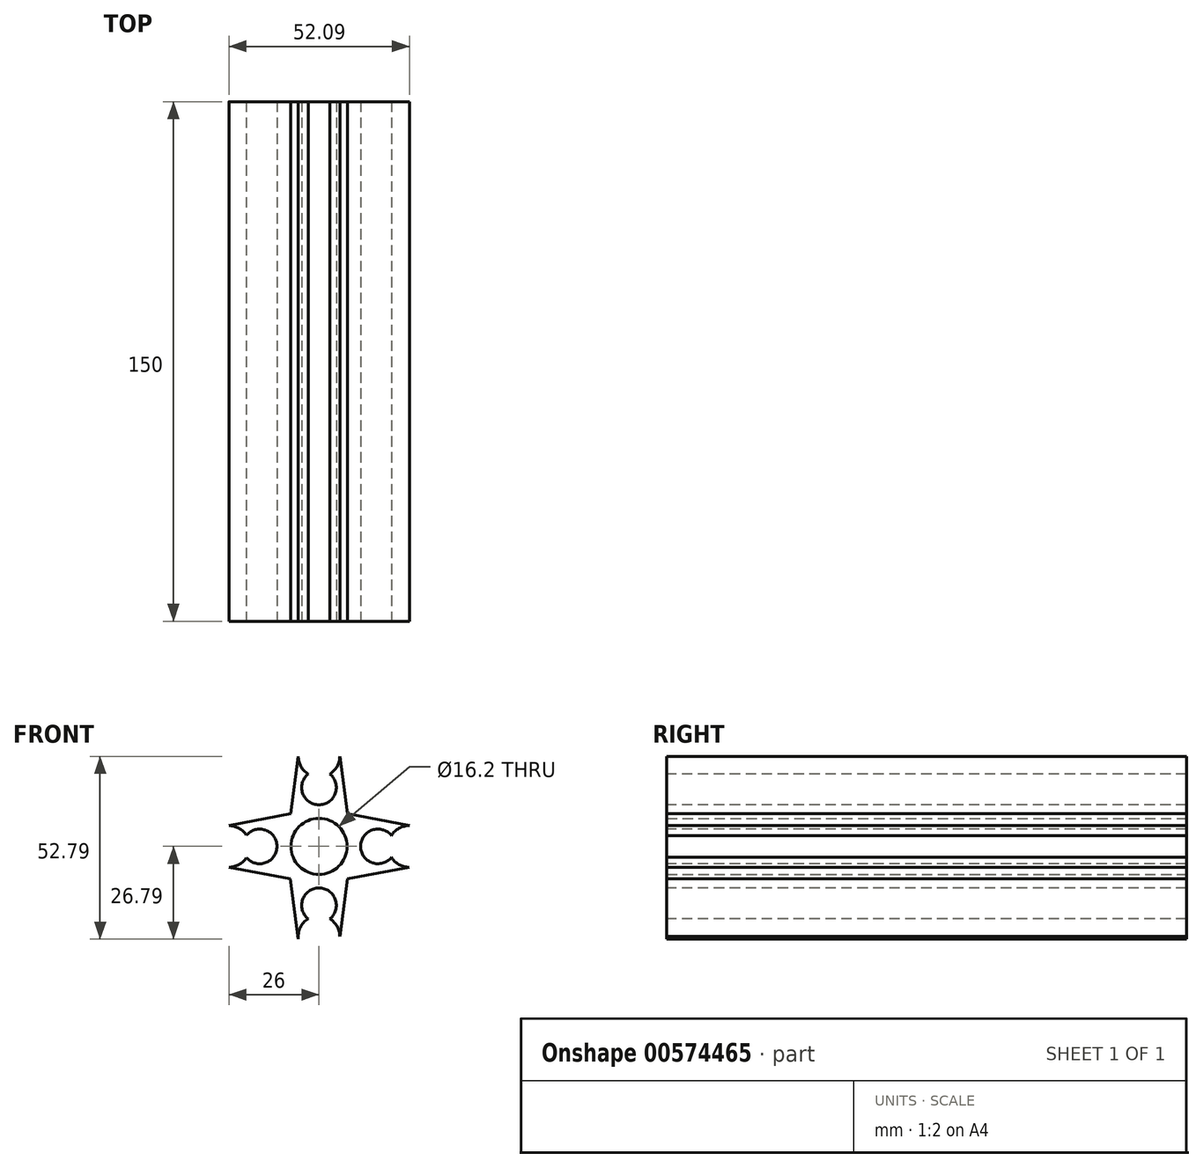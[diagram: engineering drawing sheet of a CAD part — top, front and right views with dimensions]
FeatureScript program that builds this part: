
annotation { "Feature Type Name" : "Feature", "Feature Type Description" : "" }
export const myFeature = defineFeature(function(context is Context, id is Id, definition is map)
    precondition{}
    {
        {
            var Q0;
            Q0=qCreatedBy(makeId("Front.planeOp"),FACE);
            var sketch = newSketch(context, id + "F0", { "sketchPlane" : qUnion([Q0])});
            skLineSegment(sketch, "E0", {"start": v(0, 0) * mm, "end": v(32, 0) * mm});
            skLineSegment(sketch, "E1", {"start": v(0, 0) * mm, "end": v(-32, 0) * mm});
            skLineSegment(sketch, "E2", {"start": v(0, 0) * mm, "end": v(0, 32) * mm});
            skLineSegment(sketch, "E3", {"start": v(0, 0) * mm, "end": v(0, -32) * mm});
            skCircle(sketch, "E4", {"center": v(0, 0) * mm, "radius": 8.05 * mm});
            skLineSegment(sketch, "E5", {"start": v(0, 32) * mm, "end": v(0, 26) * mm});
            skLineSegment(sketch, "E6", {"start": v(32, 0) * mm, "end": v(26, 0) * mm});
            skLineSegment(sketch, "E7", {"start": v(-32, 0) * mm, "end": v(-26, 0) * mm});
            skLineSegment(sketch, "E8", {"start": v(0, -32) * mm, "end": v(0, -26) * mm});
            skCircle(sketch, "E9", {"center": v(0, -26) * mm, "radius": 6 * mm});
            skCircle(sketch, "E10", {"center": v(26, 0) * mm, "radius": 6 * mm});
            skCircle(sketch, "E11", {"center": v(0, 0) * mm, "radius": 12.5 * mm});
            skLineSegment(sketch, "E12", {"start": v(-6, 26) * mm, "end": v(-8.17, 9.46) * mm});
            skLineSegment(sketch, "E13", {"start": v(-26, -6) * mm, "end": v(-8.26, -9.39) * mm});
            skLineSegment(sketch, "E14", {"start": v(6, -26) * mm, "end": v(8.25, -9.39) * mm});
            skLineSegment(sketch, "E15", {"start": v(8.25, -9.39) * mm, "end": v(26, -6) * mm});
            skLineSegment(sketch, "E16", {"start": v(6, 26) * mm, "end": v(8.23, 9.4) * mm});
            skCircle(sketch, "E17", {"center": v(0, 26) * mm, "radius": 6 * mm});
            skLineSegment(sketch, "E18", {"start": v(0, 0) * mm, "end": v(-14.25, 0) * mm});
            skCircle(sketch, "E19", {"center": v(-26, 0) * mm, "radius": 6 * mm});
            skLineSegment(sketch, "E20", {"start": v(-8.17, 9.46) * mm, "end": v(-25.97, 6) * mm});
            skLineSegment(sketch, "E21", {"start": v(-8.26, -9.39) * mm, "end": v(-5.95, -26.79) * mm});
            skLineSegment(sketch, "E22", {"start": v(8.23, 9.4) * mm, "end": v(26.09, 6) * mm});
            skSolve(sketch);
        }
        {
            var Q0;
            {var subQ0=sQuery(id+"F0.wireOp",EDGE,"E20");Q0=makeQuery(id+"F0.imprint","IMPRINT",FACE,{"disambiguationData":[TD([[makeQuery(id+"F0.imprint","IMPRINT",EDGE,{"derivedFrom":subQ0}),1.0]])]});}
            var Q1;
            {var subQ0=sQuery(id+"F0.wireOp",EDGE,"E7");Q1=makeQuery(id+"F0.imprint","IMPRINT",FACE,{"disambiguationData":[TD([[makeQuery(id+"F0.imprint","IMPRINT",EDGE,{"derivedFrom":subQ0}),1.0]])]});}
            var Q2;
            {var subQ0=sQuery(id+"F0.wireOp",EDGE,"E7");Q2=makeQuery(id+"F0.imprint","IMPRINT",FACE,{"disambiguationData":[TD([[makeQuery(id+"F0.imprint","IMPRINT",EDGE,{"derivedFrom":subQ0}),-1.0]])]});}
            var Q3;
            {var subQ5=sQuery(id+"F0.wireOp",EDGE,"E13");Q3=makeQuery(id+"F0.imprint","IMPRINT",FACE,{"disambiguationData":[TD([[makeQuery(id+"F0.imprint","IMPRINT",EDGE,{"derivedFrom":subQ5}),1.0]])]});}
            var Q4;
            {var subQ2=sQuery(id+"F0.wireOp",EDGE,"E3");var subQ6=sQuery(id+"F0.wireOp",EDGE,"E4");var subQ7=makeQuery(id+"F0.imprint","INTERSECT",VERTEX,{"derivedFrom":[subQ2,subQ6]});Q4=makeQuery(id+"F0.imprint","IMPRINT",FACE,{"disambiguationData":[TD([[makeQuery(id+"F0.imprint","IMPRINT",EDGE,{"disambiguationData":[TD([[subQ7,-1.0]])],"derivedFrom":subQ2}),-1.0]])]});}
            var Q5;
            {var subQ4=sQuery(id+"F0.wireOp",EDGE,"E4");var subQ5=sQuery(id+"F0.wireOp",EDGE,"E2");var subQ6=makeQuery(id+"F0.imprint","INTERSECT",VERTEX,{"derivedFrom":[subQ5,subQ4]});Q5=makeQuery(id+"F0.imprint","IMPRINT",FACE,{"disambiguationData":[TD([[makeQuery(id+"F0.imprint","IMPRINT",EDGE,{"disambiguationData":[TD([[subQ6,-1.0]])],"derivedFrom":subQ5}),1.0]])]});}
            var Q6;
            {var subQ5=sQuery(id+"F0.wireOp",EDGE,"E12");Q6=makeQuery(id+"F0.imprint","IMPRINT",FACE,{"disambiguationData":[TD([[makeQuery(id+"F0.imprint","IMPRINT",EDGE,{"derivedFrom":subQ5}),1.0]])]});}
            var Q7;
            {var subQ5=sQuery(id+"F0.wireOp",EDGE,"E16");Q7=makeQuery(id+"F0.imprint","IMPRINT",FACE,{"disambiguationData":[TD([[makeQuery(id+"F0.imprint","IMPRINT",EDGE,{"derivedFrom":subQ5}),-1.0]])]});}
            var Q8;
            {var subQ0=sQuery(id+"F0.wireOp",EDGE,"E5");Q8=makeQuery(id+"F0.imprint","IMPRINT",FACE,{"disambiguationData":[TD([[makeQuery(id+"F0.imprint","IMPRINT",EDGE,{"derivedFrom":subQ0}),1.0]])]});}
            var Q9;
            {var subQ0=sQuery(id+"F0.wireOp",EDGE,"E5");Q9=makeQuery(id+"F0.imprint","IMPRINT",FACE,{"disambiguationData":[TD([[makeQuery(id+"F0.imprint","IMPRINT",EDGE,{"derivedFrom":subQ0}),-1.0]])]});}
            var Q10;
            {var subQ5=sQuery(id+"F0.wireOp",EDGE,"E22");Q10=makeQuery(id+"F0.imprint","IMPRINT",FACE,{"disambiguationData":[TD([[makeQuery(id+"F0.imprint","IMPRINT",EDGE,{"derivedFrom":subQ5}),-1.0]])]});}
            var Q11;
            {var subQ0=sQuery(id+"F0.wireOp",EDGE,"E6");Q11=makeQuery(id+"F0.imprint","IMPRINT",FACE,{"disambiguationData":[TD([[makeQuery(id+"F0.imprint","IMPRINT",EDGE,{"derivedFrom":subQ0}),-1.0]])]});}
            var Q12;
            {var subQ0=sQuery(id+"F0.wireOp",EDGE,"E6");Q12=makeQuery(id+"F0.imprint","IMPRINT",FACE,{"disambiguationData":[TD([[makeQuery(id+"F0.imprint","IMPRINT",EDGE,{"derivedFrom":subQ0}),1.0]])]});}
            var Q13;
            {var subQ2=sQuery(id+"F0.wireOp",EDGE,"E0");var subQ4=sQuery(id+"F0.wireOp",EDGE,"E4");var subQ5=makeQuery(id+"F0.imprint","INTERSECT",VERTEX,{"derivedFrom":[subQ2,subQ4]});Q13=makeQuery(id+"F0.imprint","IMPRINT",FACE,{"disambiguationData":[TD([[makeQuery(id+"F0.imprint","IMPRINT",EDGE,{"disambiguationData":[TD([[subQ5,-1.0]])],"derivedFrom":subQ2}),1.0]])]});}
            var Q14;
            {var subQ1=sQuery(id+"F0.wireOp",EDGE,"E0");var subQ3=sQuery(id+"F0.wireOp",EDGE,"E4");var subQ4=makeQuery(id+"F0.imprint","INTERSECT",VERTEX,{"derivedFrom":[subQ1,subQ3]});Q14=makeQuery(id+"F0.imprint","IMPRINT",FACE,{"disambiguationData":[TD([[makeQuery(id+"F0.imprint","IMPRINT",EDGE,{"disambiguationData":[TD([[subQ4,-1.0]])],"derivedFrom":subQ3}),1.0]])]});}
            var Q15;
            {var subQ1=sQuery(id+"F0.wireOp",EDGE,"E2");var subQ3=sQuery(id+"F0.wireOp",EDGE,"E4");var subQ4=makeQuery(id+"F0.imprint","INTERSECT",VERTEX,{"derivedFrom":[subQ1,subQ3]});Q15=makeQuery(id+"F0.imprint","IMPRINT",FACE,{"disambiguationData":[TD([[makeQuery(id+"F0.imprint","IMPRINT",EDGE,{"disambiguationData":[TD([[subQ4,-1.0]])],"derivedFrom":subQ3}),1.0]])]});}
            var Q16;
            {var subQ1=sQuery(id+"F0.wireOp",EDGE,"E3");var subQ3=sQuery(id+"F0.wireOp",EDGE,"E4");var subQ4=makeQuery(id+"F0.imprint","INTERSECT",VERTEX,{"derivedFrom":[subQ1,subQ3]});Q16=makeQuery(id+"F0.imprint","IMPRINT",FACE,{"disambiguationData":[TD([[makeQuery(id+"F0.imprint","IMPRINT",EDGE,{"disambiguationData":[TD([[subQ4,1.0]])],"derivedFrom":subQ3}),1.0]])]});}
            var Q17;
            {var subQ1=sQuery(id+"F0.wireOp",EDGE,"E0");var subQ3=sQuery(id+"F0.wireOp",EDGE,"E4");var subQ4=makeQuery(id+"F0.imprint","INTERSECT",VERTEX,{"derivedFrom":[subQ1,subQ3]});Q17=makeQuery(id+"F0.imprint","IMPRINT",FACE,{"disambiguationData":[TD([[makeQuery(id+"F0.imprint","IMPRINT",EDGE,{"disambiguationData":[TD([[subQ4,1.0]])],"derivedFrom":subQ3}),1.0]])]});}
            var Q18;
            {var subQ0=sQuery(id+"F0.wireOp",EDGE,"E4");var subQ1=sQuery(id+"F0.wireOp",EDGE,"E0");var subQ2=makeQuery(id+"F0.imprint","INTERSECT",VERTEX,{"derivedFrom":[subQ1,subQ0]});Q18=makeQuery(id+"F0.imprint","IMPRINT",FACE,{"disambiguationData":[TD([[makeQuery(id+"F0.imprint","IMPRINT",EDGE,{"disambiguationData":[TD([[subQ2,-1.0]])],"derivedFrom":subQ1}),-1.0]])]});}
            var Q19;
            {var subQ5=sQuery(id+"F0.wireOp",EDGE,"E15");Q19=makeQuery(id+"F0.imprint","IMPRINT",FACE,{"disambiguationData":[TD([[makeQuery(id+"F0.imprint","IMPRINT",EDGE,{"derivedFrom":subQ5}),1.0]])]});}
            var Q20;
            {var subQ5=sQuery(id+"F0.wireOp",EDGE,"E21");Q20=makeQuery(id+"F0.imprint","IMPRINT",FACE,{"disambiguationData":[TD([[makeQuery(id+"F0.imprint","IMPRINT",EDGE,{"derivedFrom":subQ5}),1.0]])]});}
            var Q21;
            {var subQ5=sQuery(id+"F0.wireOp",EDGE,"E14");Q21=makeQuery(id+"F0.imprint","IMPRINT",FACE,{"disambiguationData":[TD([[makeQuery(id+"F0.imprint","IMPRINT",EDGE,{"derivedFrom":subQ5}),1.0]])]});}
            var Q22;
            {var subQ0=sQuery(id+"F0.wireOp",EDGE,"E8");Q22=makeQuery(id+"F0.imprint","IMPRINT",FACE,{"disambiguationData":[TD([[makeQuery(id+"F0.imprint","IMPRINT",EDGE,{"derivedFrom":subQ0}),1.0]])]});}
            var Q23;
            {var subQ0=sQuery(id+"F0.wireOp",EDGE,"E8");Q23=makeQuery(id+"F0.imprint","IMPRINT",FACE,{"disambiguationData":[TD([[makeQuery(id+"F0.imprint","IMPRINT",EDGE,{"derivedFrom":subQ0}),-1.0]])]});}
            extrude(context, id + "F1", {"entities" : qUnion([Q0, Q1, Q2, Q3, Q4, Q5, Q6, Q7, Q8, Q9, Q10, Q11, Q12, Q13, Q14, Q15, Q16, Q17, Q18, Q19, Q20, Q21, Q22, Q23]), "depth" : 150 * mm, "offsetDistance" : 25 * mm});
        }
        {
            var Q0;
            Q0=qCreatedBy(makeId("Front.planeOp"),FACE);
            var sketch = newSketch(context, id + "F2", { "sketchPlane" : qUnion([Q0])});
            skCircle(sketch, "E23", {"center": v(0, 0) * mm, "radius": 8.1 * mm});
            skCircle(sketch, "E24", {"center": v(0, 26) * mm, "radius": 1.6 * mm});
            skCircle(sketch, "E25", {"center": v(26, 0) * mm, "radius": 1.6 * mm});
            skCircle(sketch, "E26", {"center": v(0, -26) * mm, "radius": 1.6 * mm});
            skCircle(sketch, "E27", {"center": v(-26, 0) * mm, "radius": 1.6 * mm});
            skSolve(sketch);
        }
        {
            var Q0;
            Q0=makeQuery(id+"F2.imprint","IMPRINT",FACE,{"disambiguationData":[TD([[makeQuery(id+"F2.imprint","IMPRINT",EDGE,{"derivedFrom":sQuery(id+"F2.wireOp",EDGE,"E23")}),1.0]])]});
            var Q1;
            Q1=makeQuery(id+"F2.imprint","IMPRINT",FACE,{"disambiguationData":[TD([[makeQuery(id+"F2.imprint","IMPRINT",EDGE,{"derivedFrom":sQuery(id+"F2.wireOp",EDGE,"E24")}),1.0]])]});
            var Q2;
            Q2=makeQuery(id+"F2.imprint","IMPRINT",FACE,{"disambiguationData":[TD([[makeQuery(id+"F2.imprint","IMPRINT",EDGE,{"derivedFrom":sQuery(id+"F2.wireOp",EDGE,"E25")}),1.0]])]});
            var Q3;
            Q3=makeQuery(id+"F2.imprint","IMPRINT",FACE,{"disambiguationData":[TD([[makeQuery(id+"F2.imprint","IMPRINT",EDGE,{"derivedFrom":sQuery(id+"F2.wireOp",EDGE,"E26")}),1.0]])]});
            var Q4;
            Q4=makeQuery(id+"F2.imprint","IMPRINT",FACE,{"disambiguationData":[TD([[makeQuery(id+"F2.imprint","IMPRINT",EDGE,{"derivedFrom":sQuery(id+"F2.wireOp",EDGE,"E27")}),1.0]])]});
            extrude(context, id + "F3", {"entities" : qUnion([Q0, Q1, Q2, Q3, Q4]), "operationType" : NewBodyOperationType.REMOVE, "depth" : 155 * mm, "offsetDistance" : 25 * mm});
        }
        {
            var Q0;
            Q0=makeQuery(id+"F1.opExtrude","CAP_FACE",FACE,{"disambiguationData":[OSD([sQuery(id+"F0.wireOp",EDGE,"E9"),sQuery(id+"F0.wireOp",EDGE,"E10"),sQuery(id+"F0.wireOp",EDGE,"E12"),sQuery(id+"F0.wireOp",EDGE,"E13"),sQuery(id+"F0.wireOp",EDGE,"E14"),sQuery(id+"F0.wireOp",EDGE,"E15"),sQuery(id+"F0.wireOp",EDGE,"E16"),sQuery(id+"F0.wireOp",EDGE,"E17"),sQuery(id+"F0.wireOp",EDGE,"E19"),sQuery(id+"F0.wireOp",EDGE,"E20"),sQuery(id+"F0.wireOp",EDGE,"E21"),sQuery(id+"F0.wireOp",EDGE,"E22")])],"isStart":false});
            var sketch = newSketch(context, id + "F4", { "sketchPlane" : qUnion([Q0])});
            skCircle(sketch, "E28", {"center": v(0, -17) * mm, "radius": 5 * mm});
            skPoint(sketch, "E29.endSnap0", {"position": v(-17.13, -7.7) * mm});
            skCircle(sketch, "E30", {"center": v(-17.13, 0) * mm, "radius": 5 * mm});
            skCircle(sketch, "E31", {"center": v(0, 17) * mm, "radius": 5 * mm});
            skCircle(sketch, "E32", {"center": v(17, 0) * mm, "radius": 5 * mm});
            skSolve(sketch);
        }
        {
            var Q0;
            Q0=makeQuery(id+"F4.imprint","IMPRINT",FACE,{"disambiguationData":[TD([[makeQuery(id+"F4.imprint","IMPRINT",EDGE,{"derivedFrom":sQuery(id+"F4.wireOp",EDGE,"E30")}),1.0]])]});
            var Q1;
            Q1=makeQuery(id+"F4.imprint","IMPRINT",FACE,{"disambiguationData":[TD([[makeQuery(id+"F4.imprint","IMPRINT",EDGE,{"derivedFrom":sQuery(id+"F4.wireOp",EDGE,"E31")}),1.0]])]});
            var Q2;
            Q2=makeQuery(id+"F4.imprint","IMPRINT",FACE,{"disambiguationData":[TD([[makeQuery(id+"F4.imprint","IMPRINT",EDGE,{"derivedFrom":sQuery(id+"F4.wireOp",EDGE,"E32")}),1.0]])]});
            var Q3;
            Q3=makeQuery(id+"F4.imprint","IMPRINT",FACE,{"disambiguationData":[TD([[makeQuery(id+"F4.imprint","IMPRINT",EDGE,{"derivedFrom":sQuery(id+"F4.wireOp",EDGE,"E28")}),1.0]])]});
            extrude(context, id + "F5", {"entities" : qUnion([Q0, Q1, Q2, Q3]), "operationType" : NewBodyOperationType.REMOVE, "oppositeDirection" : true, "depth" : 155 * mm, "offsetDistance" : 25 * mm});
        }
    });
